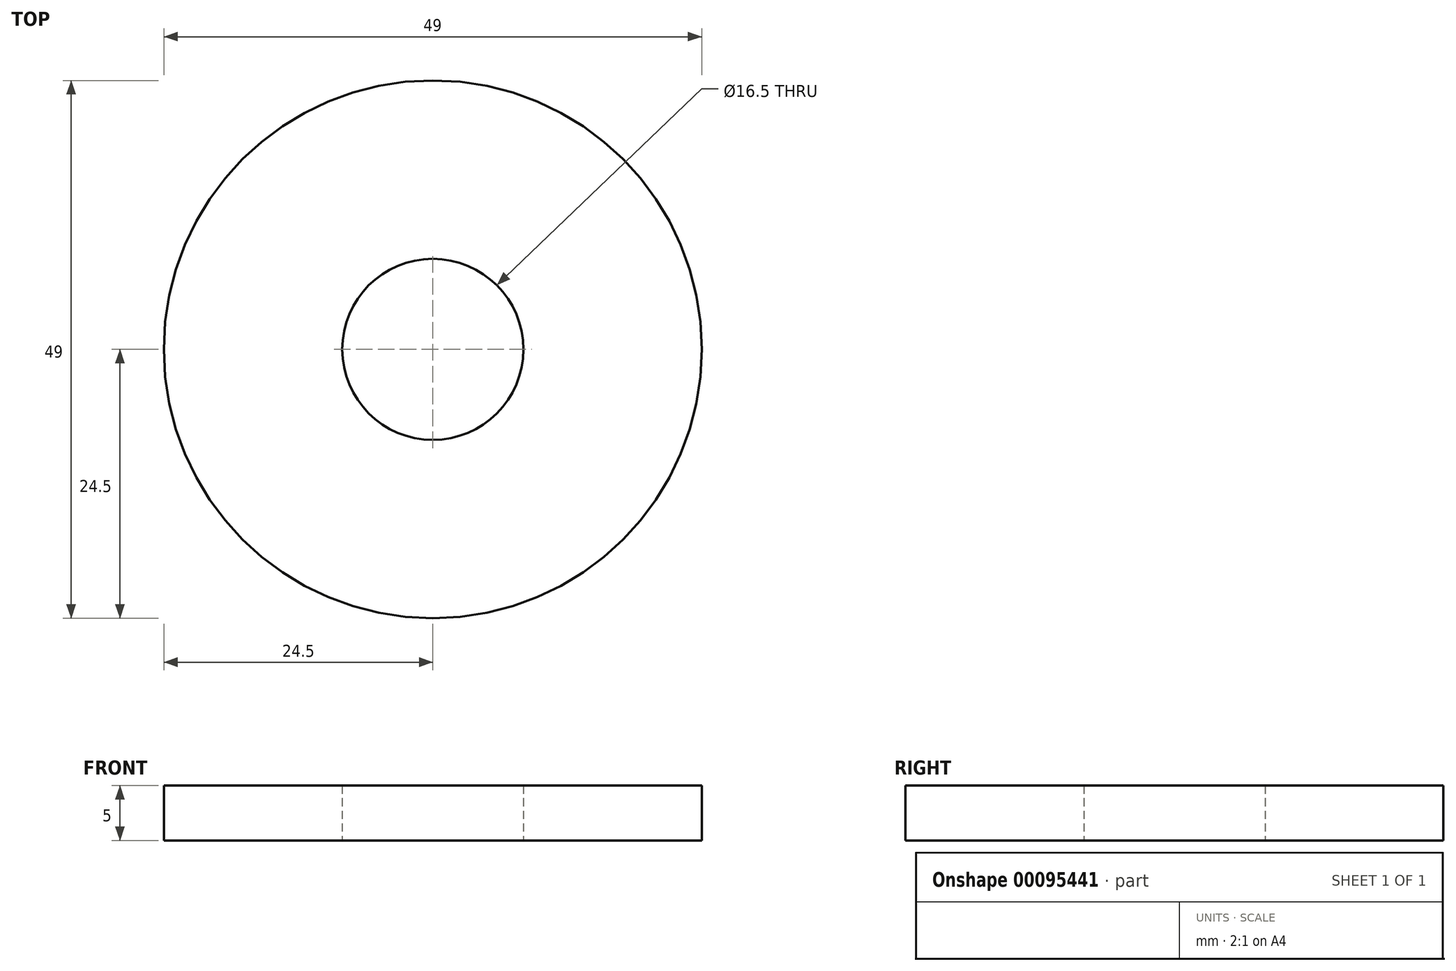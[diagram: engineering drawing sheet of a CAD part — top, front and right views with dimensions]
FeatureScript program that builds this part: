
annotation { "Feature Type Name" : "Feature", "Feature Type Description" : "" }
export const myFeature = defineFeature(function(context is Context, id is Id, definition is map)
    precondition{}
    {
        {
            var Q0;
            Q0=qCreatedBy(makeId("Top.planeOp"),FACE);
            var sketch = newSketch(context, id + "F0", { "sketchPlane" : qUnion([Q0])});
            skCircle(sketch, "E0", {"center": v(0, 0) * mm, "radius": 24.5 * mm});
            skCircle(sketch, "E1", {"center": v(0, 0) * mm, "radius": 8.25 * mm});
            skSolve(sketch);
        }
        {
            var Q0;
            Q0 = qSketchRegion(id + "F0", true);
            extrude(context, id + "F1", {"entities" : qUnion([Q0]), "depth" : 5 * mm});
        }
    });
